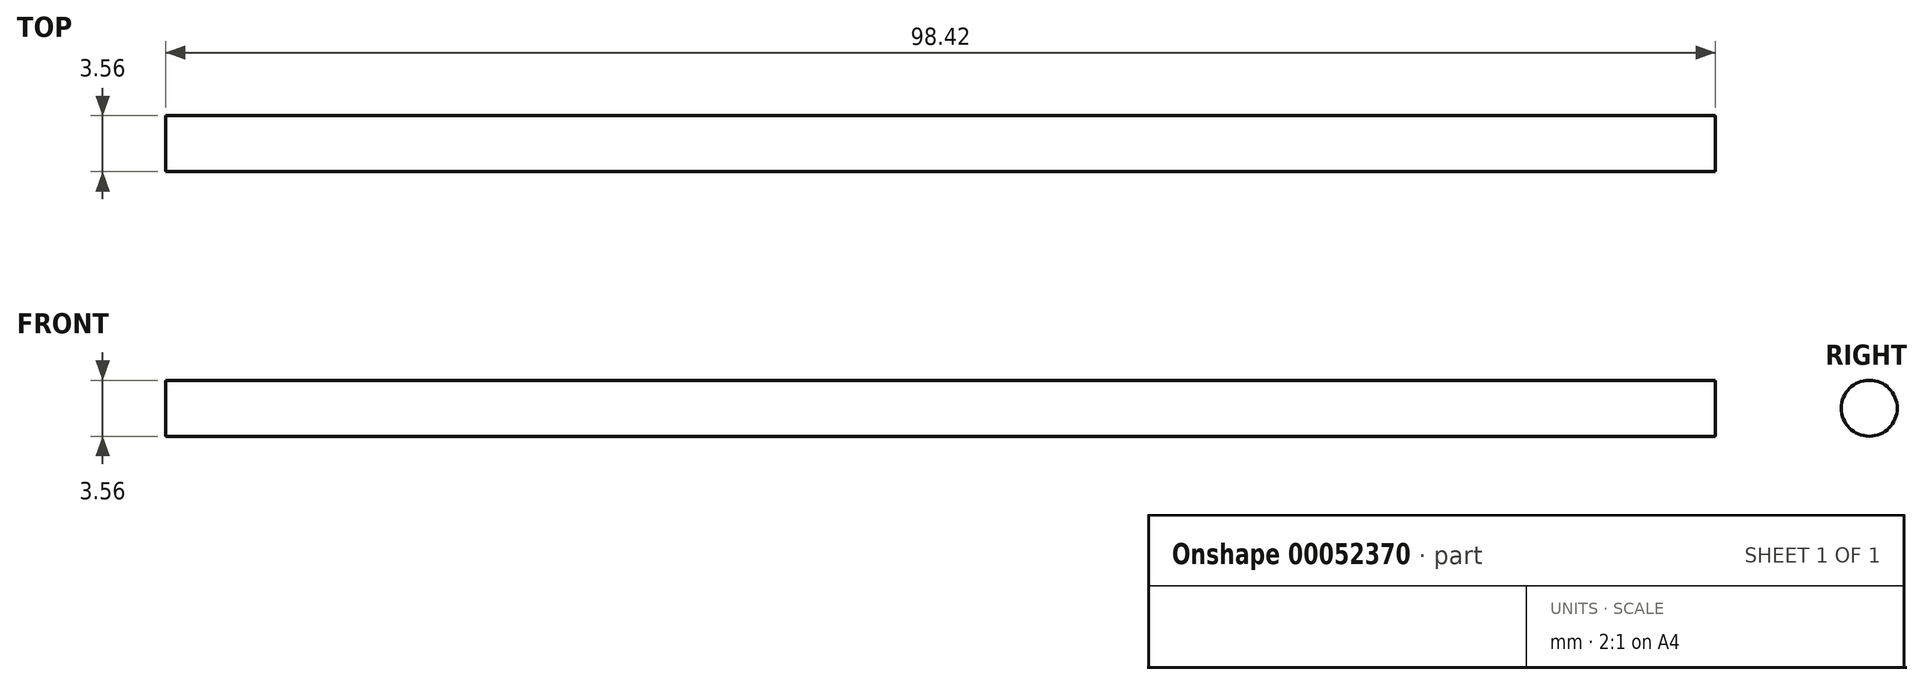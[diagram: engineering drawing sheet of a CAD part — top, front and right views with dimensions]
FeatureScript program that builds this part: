
annotation { "Feature Type Name" : "Feature", "Feature Type Description" : "" }
export const myFeature = defineFeature(function(context is Context, id is Id, definition is map)
    precondition{}
    {
        {
            var Q0;
            Q0=qCreatedBy(makeId("Right.planeOp"),FACE);
            var sketch = newSketch(context, id + "F0", { "sketchPlane" : qUnion([Q0])});
            skCircle(sketch, "E0", {"center": v(0, 0) * mm, "radius": 1.78 * mm});
            skSolve(sketch);
        }
        {
            var Q0;
            Q0 = qSketchRegion(id + "F0", true);
            extrude(context, id + "F1", {"entities" : qUnion([Q0]), "depth" : 98.42 * mm, "symmetric" : true});
        }
    });
